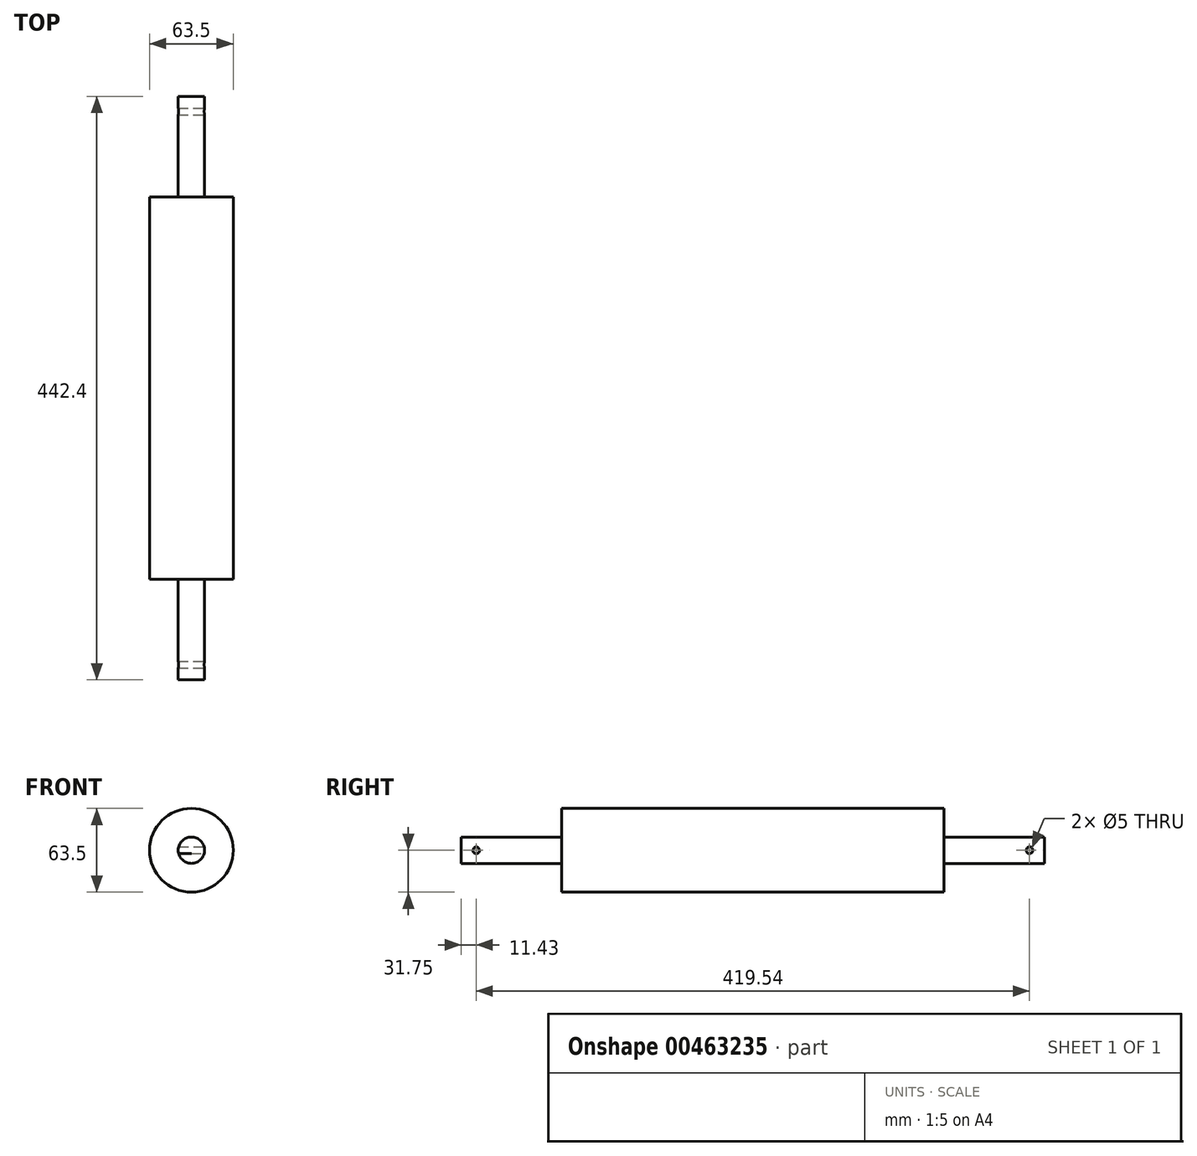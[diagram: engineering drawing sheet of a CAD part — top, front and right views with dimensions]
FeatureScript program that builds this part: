
annotation { "Feature Type Name" : "Feature", "Feature Type Description" : "" }
export const myFeature = defineFeature(function(context is Context, id is Id, definition is map)
    precondition{}
    {
        {
            var Q0;
            Q0=qCreatedBy(makeId("Front.planeOp"),FACE);
            var sketch = newSketch(context, id + "F0", { "sketchPlane" : qUnion([Q0])});
            skCircle(sketch, "E0", {"center": v(0, 0) * mm, "radius": 31.75 * mm});
            skCircle(sketch, "E1", {"center": v(0, 0) * mm, "radius": 10 * mm});
            skSolve(sketch);
        }
        {
            var Q0;
            Q0=qSketchRegion(id+"F0",true);
            var Q1;
            Q1=makeQuery(id+"F0.imprint","IMPRINT",FACE,{"disambiguationData":[TD([[makeQuery(id+"F0.imprint","IMPRINT",EDGE,{"derivedFrom":sQuery(id+"F0.wireOp",EDGE,"E1")}),1.0]])]});
            extrude(context, id + "F1", {"entities" : qUnion([Q0, Q1]), "oppositeDirection" : true, "depth" : 290 * mm});
        }
        {
            var Q0;
            Q0=makeQuery(id+"F0.imprint","IMPRINT",FACE,{"disambiguationData":[TD([[makeQuery(id+"F0.imprint","IMPRINT",EDGE,{"derivedFrom":sQuery(id+"F0.wireOp",EDGE,"E1")}),1.0]])]});
            extrude(context, id + "F2", {"entities" : qUnion([Q0]), "operationType" : NewBodyOperationType.ADD, "depth" : 76.2 * mm});
        }
        {
            var Q0;
            Q0=makeQuery(id+"F1.opExtrude","CAP_FACE",FACE,{"disambiguationData":[OSD([sQuery(id+"F0.wireOp",EDGE,"E0")])],"isStart":false});
            var sketch = newSketch(context, id + "F3", { "sketchPlane" : qUnion([Q0])});
            skCircle(sketch, "E2", {"center": v(0, 0) * mm, "radius": 10 * mm});
            skSolve(sketch);
        }
        {
            var Q0;
            Q0=qSketchRegion(id+"F3",true);
            extrude(context, id + "F4", {"entities" : qUnion([Q0]), "operationType" : NewBodyOperationType.ADD, "depth" : 76.2 * mm});
        }
        {
            var Q0;
            Q0=qCreatedBy(makeId("Right.planeOp"),FACE);
            var sketch = newSketch(context, id + "F5", { "sketchPlane" : qUnion([Q0])});
            skCircle(sketch, "E3", {"center": v(-64.77, 0) * mm, "radius": 2.5 * mm});
            skCircle(sketch, "E4", {"center": v(354.77, 0) * mm, "radius": 2.5 * mm});
            skSolve(sketch);
        }
        {
            var Q0;
            Q0=qSketchRegion(id+"F5",true);
            extrude(context, id + "F6", {"entities" : qUnion([Q0]), "operationType" : NewBodyOperationType.REMOVE, "endBound" : BoundingType.SYMMETRIC, "oppositeDirection" : true, "depth" : 127 * mm});
        }
    });
